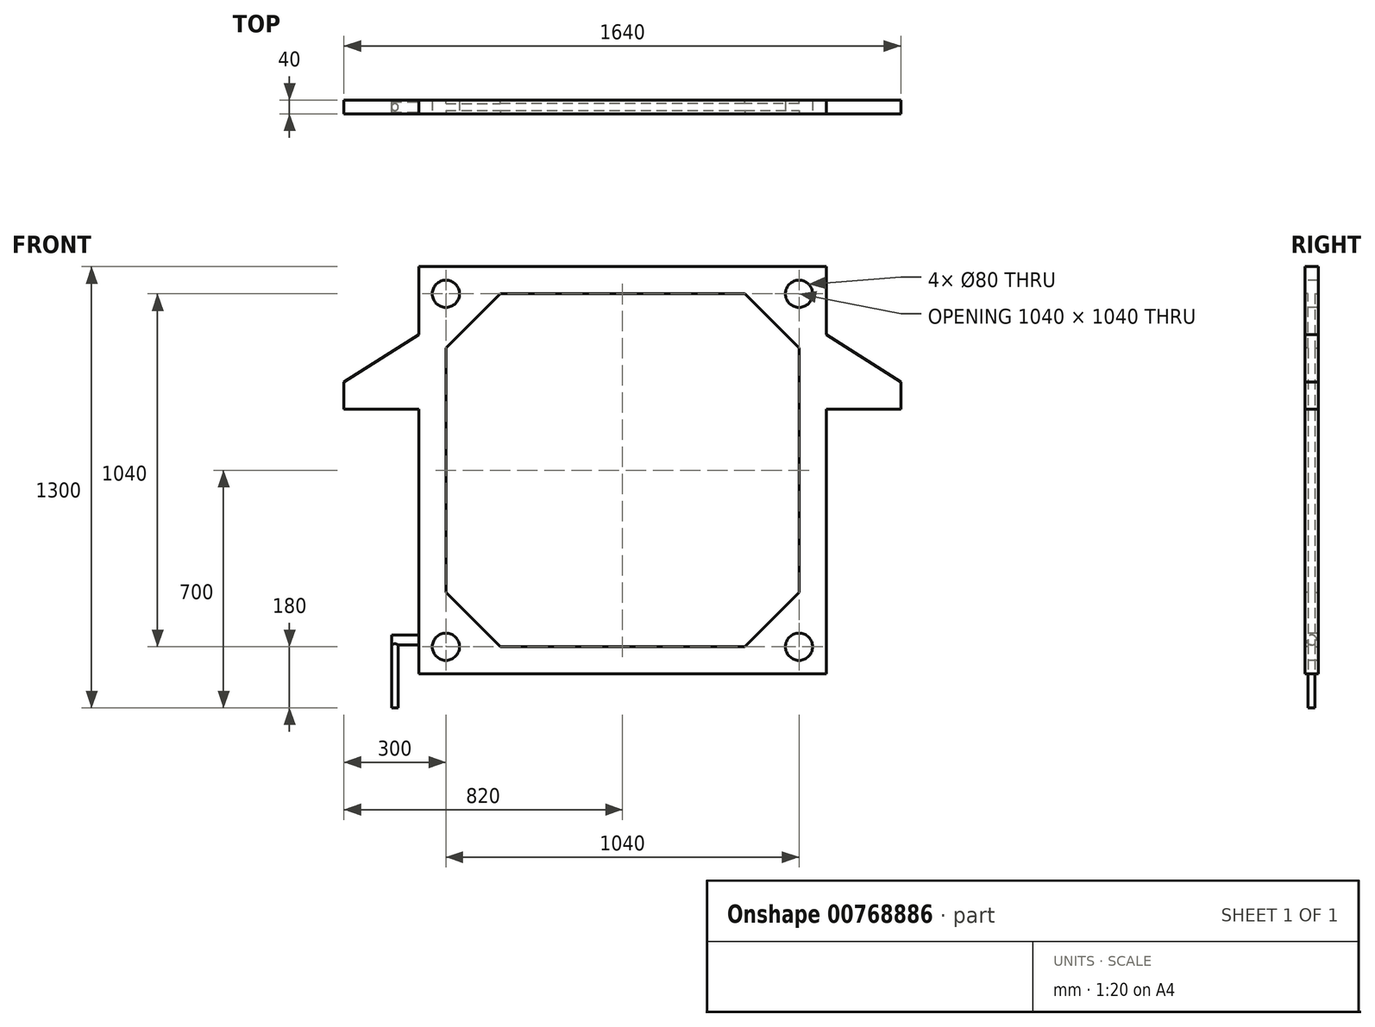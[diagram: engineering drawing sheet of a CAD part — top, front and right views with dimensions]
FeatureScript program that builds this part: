
annotation { "Feature Type Name" : "Feature", "Feature Type Description" : "" }
export const myFeature = defineFeature(function(context is Context, id is Id, definition is map)
    precondition{}
    {
        {
            var Q0;
            Q0=qCreatedBy(makeId("Front.planeOp"),FACE);
            var sketch = newSketch(context, id + "F0", { "sketchPlane" : qUnion([Q0])});
            skLineSegment(sketch, "E0.bottom", {"start": v(-600, 600) * mm, "end": v(600, 600) * mm});
            skLineSegment(sketch, "E0.top", {"start": v(-600, -600) * mm, "end": v(600, -600) * mm});
            skLineSegment(sketch, "E0.left", {"start": v(-600, 600) * mm, "end": v(-600, -600) * mm});
            skLineSegment(sketch, "E0.right", {"start": v(600, 600) * mm, "end": v(600, -600) * mm});
            skPoint(sketch, "E0.middle", {"position": v(0, 0) * mm});
            skLineSegment(sketch, "E1", {"start": v(600, 400) * mm, "end": v(820, 260) * mm});
            skLineSegment(sketch, "E2", {"start": v(820, 260) * mm, "end": v(820, 180) * mm});
            skLineSegment(sketch, "E3", {"start": v(820, 180) * mm, "end": v(600, 180) * mm});
            skLineSegment(sketch, "E4.MirrorCS", {"start": v(-820, 180) * mm, "end": v(-600, 180) * mm});
            skLineSegment(sketch, "E5.MirrorCS", {"start": v(-600, 400) * mm, "end": v(-820, 260) * mm});
            skLineSegment(sketch, "E6.MirrorCS", {"start": v(-820, 260) * mm, "end": v(-820, 180) * mm});
            skSolve(sketch);
        }
        {
            var Q0;
            Q0 = qSketchRegion(id + "F0", true);
            extrude(context, id + "F1", {"entities" : qUnion([Q0]), "endBound" : BoundingType.SYMMETRIC, "depth" : 40 * mm, "offsetDistance" : 25 * mm});
        }
        {
            var Q0;
            Q0=makeQuery(id+"F1.opExtrude","CAP_FACE",FACE,{"disambiguationData":[OSD([sQuery(id+"F0.wireOp",EDGE,"E0.bottom"),sQuery(id+"F0.wireOp",EDGE,"E0.top"),sQuery(id+"F0.wireOp",EDGE,"E0.left"),sQuery(id+"F0.wireOp",EDGE,"E0.right"),sQuery(id+"F0.wireOp",EDGE,"E1"),sQuery(id+"F0.wireOp",EDGE,"E2"),sQuery(id+"F0.wireOp",EDGE,"E3"),sQuery(id+"F0.wireOp",EDGE,"E4.MirrorCS"),sQuery(id+"F0.wireOp",EDGE,"E5.MirrorCS"),sQuery(id+"F0.wireOp",EDGE,"E6.MirrorCS")])],"isStart":false});
            var sketch = newSketch(context, id + "F2", { "sketchPlane" : qUnion([Q0])});
            skCircle(sketch, "E7", {"center": v(-520, 520) * mm, "radius": 40 * mm});
            skCircle(sketch, "E8.0.1.0", {"center": v(-520, -520) * mm, "radius": 40 * mm});
            skCircle(sketch, "E8.1.0.0", {"center": v(520, 520) * mm, "radius": 40 * mm});
            skCircle(sketch, "E8.1.1.0", {"center": v(520, -520) * mm, "radius": 40 * mm});
            skLineSegment(sketch, "E8.direction1", {"start": v(-520, 520) * mm, "end": v(520, 520) * mm, "construction": true});
            skLineSegment(sketch, "E8.direction2", {"start": v(-520, 520) * mm, "end": v(-520, -520) * mm, "construction": true});
            skSolve(sketch);
        }
        {
            var Q0;
            Q0 = qSketchRegion(id + "F2", true);
            extrude(context, id + "F3", {"entities" : qUnion([Q0]), "operationType" : NewBodyOperationType.REMOVE, "oppositeDirection" : true, "depth" : 50 * mm, "offsetDistance" : 25 * mm});
        }
        {
            var Q0;
            Q0=makeQuery(id+"F1.opExtrude","CAP_FACE",FACE,{"disambiguationData":[OSD([sQuery(id+"F0.wireOp",EDGE,"E0.bottom"),sQuery(id+"F0.wireOp",EDGE,"E0.top"),sQuery(id+"F0.wireOp",EDGE,"E0.left"),sQuery(id+"F0.wireOp",EDGE,"E0.right"),sQuery(id+"F0.wireOp",EDGE,"E1"),sQuery(id+"F0.wireOp",EDGE,"E2"),sQuery(id+"F0.wireOp",EDGE,"E3"),sQuery(id+"F0.wireOp",EDGE,"E4.MirrorCS"),sQuery(id+"F0.wireOp",EDGE,"E5.MirrorCS"),sQuery(id+"F0.wireOp",EDGE,"E6.MirrorCS")])],"isStart":false});
            var sketch = newSketch(context, id + "F4", { "sketchPlane" : qUnion([Q0])});
            skLineSegment(sketch, "E9.bottom", {"start": v(-360, 520) * mm, "end": v(360, 520) * mm});
            skLineSegment(sketch, "E9.top", {"start": v(-360, -520) * mm, "end": v(360, -520) * mm});
            skLineSegment(sketch, "E9.left", {"start": v(-520, 360) * mm, "end": v(-520, -360) * mm});
            skLineSegment(sketch, "E9.right", {"start": v(520, 360) * mm, "end": v(520, -360) * mm});
            skPoint(sketch, "E9.middle", {"position": v(0, 0) * mm});
            skLineSegment(sketch, "E10", {"start": v(-360, 520) * mm, "end": v(-520, 360) * mm});
            skLineSegment(sketch, "E11.1.0", {"start": v(-520, -360) * mm, "end": v(-360, -520) * mm});
            skLineSegment(sketch, "E11.2.0", {"start": v(360, -520) * mm, "end": v(520, -360) * mm});
            skLineSegment(sketch, "E11.3.0", {"start": v(520, 360) * mm, "end": v(360, 520) * mm});
            skPoint(sketch, "E12.orphan", {"position": v(-520, 520) * mm});
            skPoint(sketch, "E13.orphan", {"position": v(520, 520) * mm});
            skPoint(sketch, "E14.orphan", {"position": v(520, -520) * mm});
            skPoint(sketch, "E15.orphan", {"position": v(-520, -520) * mm});
            skSolve(sketch);
        }
        {
            var Q0;
            Q0=makeQuery(id+"F4.imprint","IMPRINT",FACE,{"disambiguationData":[TD([[makeQuery(id+"F4.imprint","IMPRINT",EDGE,{"derivedFrom":sQuery(id+"F4.wireOp",EDGE,"E9.bottom")}),-1.0]])]});
            extrude(context, id + "F5", {"entities" : qUnion([Q0]), "operationType" : NewBodyOperationType.REMOVE, "oppositeDirection" : true, "depth" : 10 * mm, "offsetDistance" : 25 * mm});
        }
        {
            var Q0;
            Q0=makeQuery(id+"F1.opExtrude","CAP_FACE",FACE,{"disambiguationData":[OSD([sQuery(id+"F0.wireOp",EDGE,"E0.bottom"),sQuery(id+"F0.wireOp",EDGE,"E0.top"),sQuery(id+"F0.wireOp",EDGE,"E0.left"),sQuery(id+"F0.wireOp",EDGE,"E0.right"),sQuery(id+"F0.wireOp",EDGE,"E1"),sQuery(id+"F0.wireOp",EDGE,"E2"),sQuery(id+"F0.wireOp",EDGE,"E3"),sQuery(id+"F0.wireOp",EDGE,"E4.MirrorCS"),sQuery(id+"F0.wireOp",EDGE,"E5.MirrorCS"),sQuery(id+"F0.wireOp",EDGE,"E6.MirrorCS")])],"isStart":true});
            var sketch = newSketch(context, id + "F6", { "sketchPlane" : qUnion([Q0])});
            skLineSegment(sketch, "E16.0.0", {"start": v(520, -360) * mm, "end": v(360, -520) * mm});
            skLineSegment(sketch, "E16.0.1", {"start": v(360, -520) * mm, "end": v(-360, -520) * mm});
            skLineSegment(sketch, "E16.0.2", {"start": v(-360, -520) * mm, "end": v(-520, -360) * mm});
            skLineSegment(sketch, "E16.0.3", {"start": v(-520, -360) * mm, "end": v(-520, 360) * mm});
            skLineSegment(sketch, "E16.0.4", {"start": v(-520, 360) * mm, "end": v(-360, 520) * mm});
            skLineSegment(sketch, "E16.0.5", {"start": v(-360, 520) * mm, "end": v(360, 520) * mm});
            skLineSegment(sketch, "E16.0.6", {"start": v(360, 520) * mm, "end": v(520, 360) * mm});
            skLineSegment(sketch, "E16.0.7", {"start": v(520, 360) * mm, "end": v(520, -360) * mm});
            skSolve(sketch);
        }
        {
            var Q0;
            Q0=makeQuery(id+"F6.imprint","IMPRINT",FACE,{"disambiguationData":[TD([[makeQuery(id+"F6.imprint","IMPRINT",EDGE,{"derivedFrom":sQuery(id+"F6.wireOp",EDGE,"E16.0.0")}),-1.0]])]});
            extrude(context, id + "F7", {"entities" : qUnion([Q0]), "operationType" : NewBodyOperationType.REMOVE, "oppositeDirection" : true, "depth" : 10 * mm, "offsetDistance" : 25 * mm});
        }
        {
            var Q0;
            {var subQ0=sQuery(id+"F0.wireOp",EDGE,"E0.left");Q0=makeQuery(id+"F1.opExtrude","SWEPT_FACE",FACE,{"disambiguationData":[OSD([subQ0]),TDD([makeQuery(id+"F0.imprint","IMPRINT",EDGE,{"disambiguationData":[TD([[makeQuery(id+"F0.imprint","INTERSECT",VERTEX,{"derivedFrom":[sQuery(id+"F0.wireOp",EDGE,"E0.top"),subQ0]}),1.0]])],"derivedFrom":subQ0})])]});}
            var sketch = newSketch(context, id + "F8", { "sketchPlane" : qUnion([Q0])});
            skCircle(sketch, "E17", {"center": v(0, -500) * mm, "radius": 15 * mm});
            skSolve(sketch);
        }
        {
            var Q0;
            Q0=makeQuery(id+"F8.imprint","IMPRINT",FACE,{"disambiguationData":[TD([[makeQuery(id+"F8.imprint","IMPRINT",EDGE,{"derivedFrom":sQuery(id+"F8.wireOp",EDGE,"E17")}),1.0]])]});
            extrude(context, id + "F9", {"entities" : qUnion([Q0]), "operationType" : NewBodyOperationType.ADD, "depth" : 80 * mm, "offsetDistance" : 25 * mm});
        }
        {
            var Q0;
            Q0=makeQuery(id+"F1.opExtrude","SWEPT_FACE",FACE,{"disambiguationData":[OSD([sQuery(id+"F0.wireOp",EDGE,"E0.top")])]});
            var sketch = newSketch(context, id + "F10", { "sketchPlane" : qUnion([Q0])});
            skCircle(sketch, "E18", {"center": v(-670, 0) * mm, "radius": 10 * mm});
            skSolve(sketch);
        }
        {
            var Q0;
            Q0 = qSketchRegion(id + "F10", true);
            extrude(context, id + "F11", {"entities" : qUnion([Q0]), "operationType" : NewBodyOperationType.ADD, "oppositeDirection" : true, "depth" : 100 * mm, "offsetDistance" : 25 * mm, "hasSecondDirection" : true, "secondDirectionOppositeDirection" : false, "secondDirectionDepth" : 100 * mm});
        }
    });
